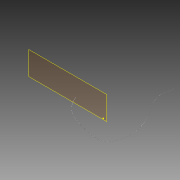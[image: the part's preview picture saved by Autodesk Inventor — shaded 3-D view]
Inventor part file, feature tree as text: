
AUTODESK INVENTOR PART (.ipt)
format: ipt  version: 2012 SP2 (Build 160219200, 219)  size: 108,544 bytes
history: native  units: in
note: dims shown in document units (in); Inventor stores cm internally (conversion verified against a paired STEP export)
features: sketch x3, plane x1, sweep x1
ambient origin geometry x8: Origin, YZ Plane, XZ Plane, XY Plane, X Axis, Y Axis, Z Axis, Center Point
bodies: Solid1 (feature_tree)
feature tree (5):
  sketch  "Sketch1"  dims[d0=0.0394in d1=0.0in]
  sketch  "3D Sketch1"
  plane  "Work Plane1"
  sweep  "Sweep1"
  sketch  "Sketch2"
